# Revit family: Котел_ТЕРМОТЕХНИК_ТТ100-01_1-20 мВт
name_source: partatom
category: Оборудование
units: mm (PartAtom-declared; Revit-internal decimal feet)

## family parameters
Всегда вертикально = Да
Классификация = Нет
На основе рабочей плоскости = Нет
Общий = Нет
При загрузке вырезать с полостями = Нет
Размер круглого соединителя = Использовать диаметр
Тип детали = Нормальный
Точка расчета площади = Нет

## types (23) — shared parameters
G = 25 мм
URL = https://www.entroros.ru
Видимость_ВКЛ = Да
Видимость_ВЫКЛ = Нет
Изготовитель = ЭНТРОРОС
Ключевая пометка = https://www.entroros.ru
Код по классификатору = D3020100
Материал_Условный BOX = <По категории>
Описание = Котел ЭНТРОРОС ТЕРМОТЕХНИК ТТ100-01
Производитель = ЭНТРОРОС
Семейство заказано = ООО ЭНТРОРОС (entroros.ru)
Семейство оборудования = ТТ100-01
Семейство разработано = ООО DASBIM (dasbim.ru)
Ссылка на документацию = https://www.entroros.ru
Штуцер_Датчик дым.газов_D = G1/2-B
Штуцер_Датчик темп. воды на входе_D = G1/2-B
Штуцер_Датчик темп. воды на выходе_D = G1/2-B
Штуцер_Люк смотровой_D = 225х160
Штуцер_Слив конденсата_D = 25 мм
Штуцер_Слив конденсата_D_Формула = G1-B
Штуцер_Тягонапоромер_D = G1/2-B
Эксплуатационный КПД (%) не менее = 94
zero-valued in all types: Стоимость, Штуцер_Люк смотровой_А

## per-type parameters (varying)
- 01_1000_ef_406: B=1540 мм; H=1768 мм; L=3183 мм; А_Дверь_Смещение наружной грани=3038 мм; Аэродин. сопротивление (Па)=256; Дверь_052=Нет; Дверь_055=Нет; Дверь_151=Нет; Дверь_153=Нет; Дверь_154=Нет; Дверь_156=Нет; Дверь_206=Да; Дверь_208=Нет; Дверь_210=Нет; Дверь_212=Нет; Дверь_213=Нет; Комментарии к типоразмеру=1.0 мВт; Корпус_151=Нет; Корпус_152=Нет; Корпус_153=Нет; Корпус_154=Нет; Корпус_155=Нет; Корпус_156=Нет; Корпус_310=Нет; Корпус_311=Нет; Корпус_312=Нет; Корпус_313=Нет; Корпус_406=Да; Корпус_408=Нет; Корпус_409=Нет; Масса наполненного котла (кг)=5190; Масса сухого котла (кг)=3326; Ном. мощность (кВт)=1000; Подключение горелки=300; С_Ось котла=910 мм; Штуцер_Вход воды_D=125 мм; Штуцер_Вход воды_А=400 мм; Штуцер_Выход воды_D=125 мм; Штуцер_Выход воды_А=1038 мм; Штуцер_Выход дыма_D=350 мм; Штуцер_Выход дыма_В=1360 мм; Штуцер_Подключение горелки=300 мм; Штуцер_Пред.клапан1_D=50 мм; Штуцер_Пред.клапан1_А=430 мм; Штуцер_Пред.клапан2_D=50 мм; Штуцер_Пред.клапан2_а=300 мм; Штуцер_Слив воды_D=40 мм; Штуцер_Слив воды_D_Формула=G1/2-B; Штуцер_Слив воды_А=0 мм; Штуцер_Слив воды_В=86 мм; Штуцер_Слив конденсата_А=0 мм; Штуцер_Слив конденсата_В=231 мм
- 02_1500_ef_407: B=1540 мм; H=1768 мм; L=3183 мм; А_Дверь_Смещение наружной грани=3038 мм; Аэродин. сопротивление (Па)=673; Дверь_052=Нет; Дверь_055=Нет; Дверь_151=Нет; Дверь_153=Нет; Дверь_154=Нет; Дверь_156=Нет; Дверь_206=Да; Дверь_208=Нет; Дверь_210=Нет; Дверь_212=Нет; Дверь_213=Нет; Комментарии к типоразмеру=1.5 мВт; Корпус_151=Нет; Корпус_152=Нет; Корпус_153=Нет; Корпус_154=Нет; Корпус_155=Нет; Корпус_156=Нет; Корпус_310=Нет; Корпус_311=Нет; Корпус_312=Нет; Корпус_313=Нет; Корпус_406=Да; Корпус_408=Нет; Корпус_409=Нет; Масса наполненного котла (кг)=5293; Масса сухого котла (кг)=3429; Ном. мощность (кВт)=1500; Подключение горелки=300; С_Ось котла=910 мм; Штуцер_Вход воды_D=125 мм; Штуцер_Вход воды_А=400 мм; Штуцер_Выход воды_D=125 мм; Штуцер_Выход воды_А=1038 мм; Штуцер_Выход дыма_D=350 мм; Штуцер_Выход дыма_В=1360 мм; Штуцер_Подключение горелки=300 мм; Штуцер_Пред.клапан1_D=50 мм; Штуцер_Пред.клапан1_А=430 мм; Штуцер_Пред.клапан2_D=50 мм; Штуцер_Пред.клапан2_а=300 мм; Штуцер_Слив воды_D=40 мм; Штуцер_Слив воды_D_Формула=G1/2-B; Штуцер_Слив воды_А=0 мм; Штуцер_Слив воды_В=86 мм; Штуцер_Слив конденсата_А=0 мм; Штуцер_Слив конденсата_В=231 мм
- 03_2000_ef_408: B=1740 мм; H=1968 мм; L=3485 мм; А_Дверь_Смещение наружной грани=3340 мм; Аэродин. сопротивление (Па)=832; Дверь_052=Нет; Дверь_055=Нет; Дверь_151=Нет; Дверь_153=Нет; Дверь_154=Нет; Дверь_156=Нет; Дверь_206=Нет; Дверь_208=Да; Дверь_210=Нет; Дверь_212=Нет; Дверь_213=Нет; Комментарии к типоразмеру=2.0 мВт; Корпус_151=Нет; Корпус_152=Нет; Корпус_153=Нет; Корпус_154=Нет; Корпус_155=Нет; Корпус_156=Нет; Корпус_310=Нет; Корпус_311=Нет; Корпус_312=Нет; Корпус_313=Нет; Корпус_406=Нет; Корпус_408=Да; Корпус_409=Нет; Масса наполненного котла (кг)=7417; Масса сухого котла (кг)=4761; Ном. мощность (кВт)=2000; Подключение горелки=380; С_Ось котла=1010 мм; Штуцер_Вход воды_D=150 мм; Штуцер_Вход воды_А=550 мм; Штуцер_Выход воды_D=150 мм; Штуцер_Выход воды_А=820 мм; Штуцер_Выход дыма_D=500 мм; Штуцер_Выход дыма_В=1520 мм; Штуцер_Подключение горелки=380 мм; Штуцер_Пред.клапан1_D=65 мм; Штуцер_Пред.клапан1_А=1205 мм; Штуцер_Пред.клапан2_D=65 мм; Штуцер_Пред.клапан2_а=300 мм; Штуцер_Слив воды_D=40 мм; Штуцер_Слив воды_D_Формула=G1/2-B; Штуцер_Слив воды_А=0 мм; Штуцер_Слив воды_В=86 мм; Штуцер_Слив конденсата_А=0 мм; Штуцер_Слив конденсата_В=232 мм
- 04_2200_ef_4081: B=1740 мм; H=1968 мм; L=3485 мм; А_Дверь_Смещение наружной грани=3340 мм; Аэродин. сопротивление (Па)=1043; Дверь_052=Нет; Дверь_055=Нет; Дверь_151=Нет; Дверь_153=Нет; Дверь_154=Нет; Дверь_156=Нет; Дверь_206=Нет; Дверь_208=Да; Дверь_210=Нет; Дверь_212=Нет; Дверь_213=Нет; Комментарии к типоразмеру=2.2 мВт; Корпус_151=Нет; Корпус_152=Нет; Корпус_153=Нет; Корпус_154=Нет; Корпус_155=Нет; Корпус_156=Нет; Корпус_310=Нет; Корпус_311=Нет; Корпус_312=Нет; Корпус_313=Нет; Корпус_406=Нет; Корпус_408=Да; Корпус_409=Нет; Масса наполненного котла (кг)=7566; Масса сухого котла (кг)=4909; Ном. мощность (кВт)=2200; Подключение горелки=380; С_Ось котла=1010 мм; Штуцер_Вход воды_D=150 мм; Штуцер_Вход воды_А=550 мм; Штуцер_Выход воды_D=150 мм; Штуцер_Выход воды_А=820 мм; Штуцер_Выход дыма_D=500 мм; Штуцер_Выход дыма_В=1520 мм; Штуцер_Подключение горелки=380 мм; Штуцер_Пред.клапан1_D=65 мм; Штуцер_Пред.клапан1_А=1205 мм; Штуцер_Пред.клапан2_D=65 мм; Штуцер_Пред.клапан2_а=300 мм; Штуцер_Слив воды_D=40 мм; Штуцер_Слив воды_D_Формула=G1/2-B; Штуцер_Слив воды_А=0 мм; Штуцер_Слив воды_В=86 мм; Штуцер_Слив конденсата_А=0 мм; Штуцер_Слив конденсата_В=232 мм
- 05_2500_ef_409: B=1740 мм; H=1968 мм; L=3735 мм; А_Дверь_Смещение наружной грани=3590 мм; Аэродин. сопротивление (Па)=1030; Дверь_052=Нет; Дверь_055=Нет; Дверь_151=Нет; Дверь_153=Нет; Дверь_154=Нет; Дверь_156=Нет; Дверь_206=Нет; Дверь_208=Да; Дверь_210=Нет; Дверь_212=Нет; Дверь_213=Нет; Комментарии к типоразмеру=2.5 мВт; Корпус_151=Нет; Корпус_152=Нет; Корпус_153=Нет; Корпус_154=Нет; Корпус_155=Нет; Корпус_156=Нет; Корпус_310=Нет; Корпус_311=Нет; Корпус_312=Нет; Корпус_313=Нет; Корпус_406=Нет; Корпус_408=Нет; Корпус_409=Да; Масса наполненного котла (кг)=8124; Масса сухого котла (кг)=5385; Ном. мощность (кВт)=2500; Подключение горелки=380; С_Ось котла=1010 мм; Штуцер_Вход воды_D=150 мм; Штуцер_Вход воды_А=550 мм; Штуцер_Выход воды_D=150 мм; Штуцер_Выход воды_А=875 мм; Штуцер_Выход дыма_D=500 мм; Штуцер_Выход дыма_В=1520 мм; Штуцер_Подключение горелки=380 мм; Штуцер_Пред.клапан1_D=65 мм; Штуцер_Пред.клапан1_А=1400 мм; Штуцер_Пред.клапан2_D=65 мм; Штуцер_Пред.клапан2_а=300 мм; Штуцер_Слив воды_D=40 мм; Штуцер_Слив воды_D_Формула=G1/2-B; Штуцер_Слив воды_А=0 мм; Штуцер_Слив воды_В=86 мм; Штуцер_Слив конденсата_А=0 мм; Штуцер_Слив конденсата_В=232 мм
- 06_3000_ef_310: B=1940 мм; H=2168 мм; L=4134 мм; А_Дверь_Смещение наружной грани=3978 мм; Аэродин. сопротивление (Па)=895; Дверь_052=Нет; Дверь_055=Нет; Дверь_151=Нет; Дверь_153=Нет; Дверь_154=Нет; Дверь_156=Нет; Дверь_206=Нет; Дверь_208=Нет; Дверь_210=Да; Дверь_212=Нет; Дверь_213=Нет; Комментарии к типоразмеру=3.0 мВт; Корпус_151=Нет; Корпус_152=Нет; Корпус_153=Нет; Корпус_154=Нет; Корпус_155=Нет; Корпус_156=Нет; Корпус_310=Да; Корпус_311=Нет; Корпус_312=Нет; Корпус_313=Нет; Корпус_406=Нет; Корпус_408=Нет; Корпус_409=Нет; Масса наполненного котла (кг)=10993; Масса сухого котла (кг)=7102; Ном. мощность (кВт)=3000; Подключение горелки=450; С_Ось котла=1110 мм; Штуцер_Вход воды_D=200 мм; Штуцер_Вход воды_А=600 мм; Штуцер_Выход воды_D=200 мм; Штуцер_Выход воды_А=963 мм; Штуцер_Выход дыма_D=500 мм; Штуцер_Выход дыма_В=1720 мм; Штуцер_Подключение горелки=450 мм; Штуцер_Пред.клапан1_D=65 мм; Штуцер_Пред.клапан1_А=1600 мм; Штуцер_Пред.клапан2_D=65 мм; Штуцер_Пред.клапан2_а=300 мм; Штуцер_Слив воды_D=40 мм; Штуцер_Слив воды_D_Формула=G1/2-B; Штуцер_Слив воды_А=0 мм; Штуцер_Слив воды_В=116 мм; Штуцер_Слив конденсата_А=0 мм; Штуцер_Слив конденсата_В=233 мм
- 07_3200_ef_3101: B=1940 мм; H=2168 мм; L=4134 мм; А_Дверь_Смещение наружной грани=3978 мм; Аэродин. сопротивление (Па)=1046; Дверь_052=Нет; Дверь_055=Нет; Дверь_151=Нет; Дверь_153=Нет; Дверь_154=Нет; Дверь_156=Нет; Дверь_206=Нет; Дверь_208=Нет; Дверь_210=Да; Дверь_212=Нет; Дверь_213=Нет; Комментарии к типоразмеру=3.2 мВт; Корпус_151=Нет; Корпус_152=Нет; Корпус_153=Нет; Корпус_154=Нет; Корпус_155=Нет; Корпус_156=Нет; Корпус_310=Да; Корпус_311=Нет; Корпус_312=Нет; Корпус_313=Нет; Корпус_406=Нет; Корпус_408=Нет; Корпус_409=Нет; Масса наполненного котла (кг)=11213; Масса сухого котла (кг)=7322; Ном. мощность (кВт)=3200; Подключение горелки=450; С_Ось котла=1110 мм; Штуцер_Вход воды_D=200 мм; Штуцер_Вход воды_А=600 мм; Штуцер_Выход воды_D=200 мм; Штуцер_Выход воды_А=963 мм; Штуцер_Выход дыма_D=500 мм; Штуцер_Выход дыма_В=1720 мм; Штуцер_Подключение горелки=450 мм; Штуцер_Пред.клапан1_D=65 мм; Штуцер_Пред.клапан1_А=1600 мм; Штуцер_Пред.клапан2_D=65 мм; Штуцер_Пред.клапан2_а=300 мм; Штуцер_Слив воды_D=40 мм; Штуцер_Слив воды_D_Формула=G1/2-B; Штуцер_Слив воды_А=0 мм; Штуцер_Слив воды_В=116 мм; Штуцер_Слив конденсата_А=0 мм; Штуцер_Слив конденсата_В=233 мм
- 08_3500_ef_311: B=1940 мм; H=2168 мм; L=4532 мм; А_Дверь_Смещение наружной грани=4378 мм; Аэродин. сопротивление (Па)=1245; Дверь_052=Нет; Дверь_055=Нет; Дверь_151=Нет; Дверь_153=Нет; Дверь_154=Нет; Дверь_156=Нет; Дверь_206=Нет; Дверь_208=Нет; Дверь_210=Да; Дверь_212=Нет; Дверь_213=Нет; Комментарии к типоразмеру=3.5 мВт; Корпус_151=Нет; Корпус_152=Нет; Корпус_153=Нет; Корпус_154=Нет; Корпус_155=Нет; Корпус_156=Нет; Корпус_310=Нет; Корпус_311=Да; Корпус_312=Нет; Корпус_313=Нет; Корпус_406=Нет; Корпус_408=Нет; Корпус_409=Нет; Масса наполненного котла (кг)=12363; Масса сухого котла (кг)=7971; Ном. мощность (кВт)=3500; Подключение горелки=450; С_Ось котла=1110 мм; Штуцер_Вход воды_D=200 мм; Штуцер_Вход воды_А=600 мм; Штуцер_Выход воды_D=200 мм; Штуцер_Выход воды_А=1013 мм; Штуцер_Выход дыма_D=500 мм; Штуцер_Выход дыма_В=1720 мм; Штуцер_Подключение горелки=450 мм; Штуцер_Пред.клапан1_D=65 мм; Штуцер_Пред.клапан1_А=1950 мм; Штуцер_Пред.клапан2_D=65 мм; Штуцер_Пред.клапан2_а=300 мм; Штуцер_Слив воды_D=40 мм; Штуцер_Слив воды_D_Формула=G1/2-B; Штуцер_Слив воды_А=0 мм; Штуцер_Слив воды_В=116 мм; Штуцер_Слив конденсата_А=0 мм; Штуцер_Слив конденсата_В=233 мм
- 09_4200_ef_312: B=2100 мм; H=2328 мм; L=4831 мм; А_Дверь_Смещение наружной грани=4674 мм; Аэродин. сопротивление (Па)=1213; Дверь_052=Нет; Дверь_055=Нет; Дверь_151=Нет; Дверь_153=Нет; Дверь_154=Нет; Дверь_156=Нет; Дверь_206=Нет; Дверь_208=Нет; Дверь_210=Нет; Дверь_212=Да; Дверь_213=Нет; Комментарии к типоразмеру=4.2 мВт; Корпус_151=Нет; Корпус_152=Нет; Корпус_153=Нет; Корпус_154=Нет; Корпус_155=Нет; Корпус_156=Нет; Корпус_310=Нет; Корпус_311=Нет; Корпус_312=Да; Корпус_313=Нет; Корпус_406=Нет; Корпус_408=Нет; Корпус_409=Нет; Масса наполненного котла (кг)=14921; Масса сухого котла (кг)=7980; Ном. мощность (кВт)=4200; Подключение горелки=450; С_Ось котла=1205 мм; Штуцер_Вход воды_D=200 мм; Штуцер_Вход воды_А=700 мм; Штуцер_Выход воды_D=200 мм; Штуцер_Выход воды_А=959 мм; Штуцер_Выход дыма_D=650 мм; Штуцер_Выход дыма_В=1805 мм; Штуцер_Подключение горелки=450 мм; Штуцер_Пред.клапан1_D=80 мм; Штуцер_Пред.клапан1_А=2100 мм; Штуцер_Пред.клапан2_D=80 мм; Штуцер_Пред.клапан2_а=300 мм; Штуцер_Слив воды_D=40 мм; Штуцер_Слив воды_D_Формула=G1/2-B; Штуцер_Слив воды_А=0 мм; Штуцер_Слив воды_В=119 мм; Штуцер_Слив конденсата_А=0 мм; Штуцер_Слив конденсата_В=266 мм
- 10_5000_ef_3121: B=2100 мм; H=2328 мм; L=4831 мм; А_Дверь_Смещение наружной грани=4674 мм; Аэродин. сопротивление (Па)=1806; Дверь_052=Нет; Дверь_055=Нет; Дверь_151=Нет; Дверь_153=Нет; Дверь_154=Нет; Дверь_156=Нет; Дверь_206=Нет; Дверь_208=Нет; Дверь_210=Нет; Дверь_212=Да; Дверь_213=Нет; Комментарии к типоразмеру=5.0 мВт; Корпус_151=Нет; Корпус_152=Нет; Корпус_153=Нет; Корпус_154=Нет; Корпус_155=Нет; Корпус_156=Нет; Корпус_310=Нет; Корпус_311=Нет; Корпус_312=Да; Корпус_313=Нет; Корпус_406=Нет; Корпус_408=Нет; Корпус_409=Нет; Масса наполненного котла (кг)=15201; Масса сухого котла (кг)=10083; Ном. мощность (кВт)=5000; Подключение горелки=450; С_Ось котла=1205 мм; Штуцер_Вход воды_D=200 мм; Штуцер_Вход воды_А=700 мм; Штуцер_Выход воды_D=200 мм; Штуцер_Выход воды_А=959 мм; Штуцер_Выход дыма_D=650 мм; Штуцер_Выход дыма_В=1805 мм; Штуцер_Подключение горелки=450 мм; Штуцер_Пред.клапан1_D=80 мм; Штуцер_Пред.клапан1_А=2100 мм; Штуцер_Пред.клапан2_D=80 мм; Штуцер_Пред.клапан2_а=300 мм; Штуцер_Слив воды_D=40 мм; Штуцер_Слив воды_D_Формула=G1/2-B; Штуцер_Слив воды_А=0 мм; Штуцер_Слив воды_В=119 мм; Штуцер_Слив конденсата_А=0 мм; Штуцер_Слив конденсата_В=266 мм
- 11_5400_ef_313: B=2200 мм; H=2438 мм; L=5103 мм; А_Дверь_Смещение наружной грани=4963 мм; Аэродин. сопротивление (Па)=1058; Дверь_052=Нет; Дверь_055=Нет; Дверь_151=Нет; Дверь_153=Нет; Дверь_154=Нет; Дверь_156=Нет; Дверь_206=Нет; Дверь_208=Нет; Дверь_210=Нет; Дверь_212=Нет; Дверь_213=Да; Комментарии к типоразмеру=5.4 мВт; Корпус_151=Нет; Корпус_152=Нет; Корпус_153=Нет; Корпус_154=Нет; Корпус_155=Нет; Корпус_156=Нет; Корпус_310=Нет; Корпус_311=Нет; Корпус_312=Нет; Корпус_313=Да; Корпус_406=Нет; Корпус_408=Нет; Корпус_409=Нет; Масса наполненного котла (кг)=16781; Масса сухого котла (кг)=11247; Ном. мощность (кВт)=5400; Подключение горелки=450; С_Ось котла=1262 мм; Штуцер_Вход воды_D=250 мм; Штуцер_Вход воды_А=800 мм; Штуцер_Выход воды_D=250 мм; Штуцер_Выход воды_А=1146 мм; Штуцер_Выход дыма_D=650 мм; Штуцер_Выход дыма_В=1890 мм; Штуцер_Подключение горелки=450 мм; Штуцер_Пред.клапан1_D=80 мм; Штуцер_Пред.клапан1_А=2100 мм; Штуцер_Пред.клапан2_D=80 мм; Штуцер_Пред.клапан2_а=300 мм; Штуцер_Слив воды_D=50 мм; Штуцер_Слив воды_D_Формула=50; Штуцер_Слив воды_А=0 мм; Штуцер_Слив воды_В=139 мм; Штуцер_Слив конденсата_А=0 мм; Штуцер_Слив конденсата_В=263 мм
- 12_6000_ef_3131: B=2200 мм; H=2438 мм; L=5103 мм; А_Дверь_Смещение наружной грани=4963 мм; Аэродин. сопротивление (Па)=1352; Дверь_052=Нет; Дверь_055=Нет; Дверь_151=Нет; Дверь_153=Нет; Дверь_154=Нет; Дверь_156=Нет; Дверь_206=Нет; Дверь_208=Нет; Дверь_210=Нет; Дверь_212=Нет; Дверь_213=Да; Комментарии к типоразмеру=6.0 мВт; Корпус_151=Нет; Корпус_152=Нет; Корпус_153=Нет; Корпус_154=Нет; Корпус_155=Нет; Корпус_156=Нет; Корпус_310=Нет; Корпус_311=Нет; Корпус_312=Нет; Корпус_313=Да; Корпус_406=Нет; Корпус_408=Нет; Корпус_409=Нет; Масса наполненного котла (кг)=17572; Масса сухого котла (кг)=11595; Ном. мощность (кВт)=6000; Подключение горелки=450; С_Ось котла=1262 мм; Штуцер_Вход воды_D=250 мм; Штуцер_Вход воды_А=800 мм; Штуцер_Выход воды_D=250 мм; Штуцер_Выход воды_А=1146 мм; Штуцер_Выход дыма_D=650 мм; Штуцер_Выход дыма_В=1890 мм; Штуцер_Подключение горелки=450 мм; Штуцер_Пред.клапан1_D=80 мм; Штуцер_Пред.клапан1_А=2100 мм; Штуцер_Пред.клапан2_D=80 мм; Штуцер_Пред.клапан2_а=300 мм; Штуцер_Слив воды_D=50 мм; Штуцер_Слив воды_D_Формула=50; Штуцер_Слив воды_А=0 мм; Штуцер_Слив воды_В=139 мм; Штуцер_Слив конденсата_А=0 мм; Штуцер_Слив конденсата_В=263 мм
- 13_6500_ef_151: B=2360 мм; H=2574 мм; L=5412 мм; А_Дверь_Смещение наружной грани=5261 мм; Аэродин. сопротивление (Па)=1123; Дверь_052=Нет; Дверь_055=Нет; Дверь_151=Да; Дверь_153=Нет; Дверь_154=Нет; Дверь_156=Нет; Дверь_206=Нет; Дверь_208=Нет; Дверь_210=Нет; Дверь_212=Нет; Дверь_213=Нет; Комментарии к типоразмеру=6.5 мВт; Корпус_151=Да; Корпус_152=Нет; Корпус_153=Нет; Корпус_154=Нет; Корпус_155=Нет; Корпус_156=Нет; Корпус_310=Нет; Корпус_311=Нет; Корпус_312=Нет; Корпус_313=Нет; Корпус_406=Нет; Корпус_408=Нет; Корпус_409=Нет; Масса наполненного котла (кг)=21299; Масса сухого котла (кг)=14071; Ном. мощность (кВт)=6500; Подключение горелки=500; С_Ось котла=1314 мм; Штуцер_Вход воды_D=250 мм; Штуцер_Вход воды_А=900 мм; Штуцер_Выход воды_D=250 мм; Штуцер_Выход воды_А=1134 мм; Штуцер_Выход дыма_D=800 мм; Штуцер_Выход дыма_В=1970 мм; Штуцер_Подключение горелки=500 мм; Штуцер_Пред.клапан1_D=100 мм; Штуцер_Пред.клапан1_А=1970 мм; Штуцер_Пред.клапан2_D=100 мм; Штуцер_Пред.клапан2_а=370 мм; Штуцер_Слив воды_D=50 мм; Штуцер_Слив воды_D_Формула=50; Штуцер_Слив воды_А=91 мм; Штуцер_Слив воды_В=120 мм; Штуцер_Слив конденсата_А=0 мм; Штуцер_Слив конденсата_В=236 мм
- 14_7000_ef_1511: B=2360 мм; H=2574 мм; L=5412 мм; А_Дверь_Смещение наружной грани=5261 мм; Аэродин. сопротивление (Па)=1335; Дверь_052=Нет; Дверь_055=Нет; Дверь_151=Да; Дверь_153=Нет; Дверь_154=Нет; Дверь_156=Нет; Дверь_206=Нет; Дверь_208=Нет; Дверь_210=Нет; Дверь_212=Нет; Дверь_213=Нет; Комментарии к типоразмеру=7.0 мВт; Корпус_151=Да; Корпус_152=Нет; Корпус_153=Нет; Корпус_154=Нет; Корпус_155=Нет; Корпус_156=Нет; Корпус_310=Нет; Корпус_311=Нет; Корпус_312=Нет; Корпус_313=Нет; Корпус_406=Нет; Корпус_408=Нет; Корпус_409=Нет; Масса наполненного котла (кг)=21735; Масса сухого котла (кг)=14507; Ном. мощность (кВт)=7000; Подключение горелки=500; С_Ось котла=1314 мм; Штуцер_Вход воды_D=250 мм; Штуцер_Вход воды_А=900 мм; Штуцер_Выход воды_D=250 мм; Штуцер_Выход воды_А=1134 мм; Штуцер_Выход дыма_D=800 мм; Штуцер_Выход дыма_В=1970 мм; Штуцер_Подключение горелки=500 мм; Штуцер_Пред.клапан1_D=100 мм; Штуцер_Пред.клапан1_А=1970 мм; Штуцер_Пред.клапан2_D=100 мм; Штуцер_Пред.клапан2_а=370 мм; Штуцер_Слив воды_D=50 мм; Штуцер_Слив воды_D_Формула=50; Штуцер_Слив воды_А=91 мм; Штуцер_Слив воды_В=120 мм; Штуцер_Слив конденсата_А=0 мм; Штуцер_Слив конденсата_В=236 мм
- 15_8000_ef_152: B=2500 мм; H=2710 мм; L=5805 мм; А_Дверь_Смещение наружной грани=5648 мм; Аэродин. сопротивление (Па)=1251; Дверь_052=Да; Дверь_055=Нет; Дверь_151=Нет; Дверь_153=Нет; Дверь_154=Нет; Дверь_156=Нет; Дверь_206=Нет; Дверь_208=Нет; Дверь_210=Нет; Дверь_212=Нет; Дверь_213=Нет; Комментарии к типоразмеру=8.0 мВт; Корпус_151=Нет; Корпус_152=Да; Корпус_153=Нет; Корпус_154=Нет; Корпус_155=Нет; Корпус_156=Нет; Корпус_310=Нет; Корпус_311=Нет; Корпус_312=Нет; Корпус_313=Нет; Корпус_406=Нет; Корпус_408=Нет; Корпус_409=Нет; Масса наполненного котла (кг)=25867; Масса сухого котла (кг)=16961; Ном. мощность (кВт)=8000; Подключение горелки=590; С_Ось котла=1370 мм; Штуцер_Вход воды_D=300 мм; Штуцер_Вход воды_А=1000 мм; Штуцер_Выход воды_D=300 мм; Штуцер_Выход воды_А=1215 мм; Штуцер_Выход дыма_D=800 мм; Штуцер_Выход дыма_В=2070 мм; Штуцер_Подключение горелки=590 мм; Штуцер_Пред.клапан1_D=100 мм; Штуцер_Пред.клапан1_А=1990 мм; Штуцер_Пред.клапан2_D=100 мм; Штуцер_Пред.клапан2_а=500 мм; Штуцер_Слив воды_D=50 мм; Штуцер_Слив воды_D_Формула=50; Штуцер_Слив воды_А=0 мм; Штуцер_Слив воды_В=82 мм; Штуцер_Слив конденсата_А=0 мм; Штуцер_Слив конденсата_В=213 мм
- 16_8700_ef_1521: B=2500 мм; H=2710 мм; L=5805 мм; А_Дверь_Смещение наружной грани=5648 мм; Аэродин. сопротивление (Па)=1524; Дверь_052=Да; Дверь_055=Нет; Дверь_151=Нет; Дверь_153=Нет; Дверь_154=Нет; Дверь_156=Нет; Дверь_206=Нет; Дверь_208=Нет; Дверь_210=Нет; Дверь_212=Нет; Дверь_213=Нет; Комментарии к типоразмеру=8.7 мВт; Корпус_151=Нет; Корпус_152=Да; Корпус_153=Нет; Корпус_154=Нет; Корпус_155=Нет; Корпус_156=Нет; Корпус_310=Нет; Корпус_311=Нет; Корпус_312=Нет; Корпус_313=Нет; Корпус_406=Нет; Корпус_408=Нет; Корпус_409=Нет; Масса наполненного котла (кг)=26219; Масса сухого котла (кг)=17486; Ном. мощность (кВт)=8700; Подключение горелки=590; С_Ось котла=1370 мм; Штуцер_Вход воды_D=300 мм; Штуцер_Вход воды_А=1000 мм; Штуцер_Выход воды_D=300 мм; Штуцер_Выход воды_А=1215 мм; Штуцер_Выход дыма_D=800 мм; Штуцер_Выход дыма_В=2070 мм; Штуцер_Подключение горелки=590 мм; Штуцер_Пред.клапан1_D=100 мм; Штуцер_Пред.клапан1_А=1990 мм; Штуцер_Пред.клапан2_D=100 мм; Штуцер_Пред.клапан2_а=500 мм; Штуцер_Слив воды_D=50 мм; Штуцер_Слив воды_D_Формула=50; Штуцер_Слив воды_А=0 мм; Штуцер_Слив воды_В=82 мм; Штуцер_Слив конденсата_А=0 мм; Штуцер_Слив конденсата_В=213 мм
- 17_10000_ef_153: B=2680 мм; H=2862 мм; L=6440 мм; А_Дверь_Смещение наружной грани=6290 мм; Аэродин. сопротивление (Па)=1461; Дверь_052=Нет; Дверь_055=Нет; Дверь_151=Нет; Дверь_153=Да; Дверь_154=Нет; Дверь_156=Нет; Дверь_206=Нет; Дверь_208=Нет; Дверь_210=Нет; Дверь_212=Нет; Дверь_213=Нет; Комментарии к типоразмеру=10.0 мВт; Корпус_151=Нет; Корпус_152=Нет; Корпус_153=Да; Корпус_154=Нет; Корпус_155=Нет; Корпус_156=Нет; Корпус_310=Нет; Корпус_311=Нет; Корпус_312=Нет; Корпус_313=Нет; Корпус_406=Нет; Корпус_408=Нет; Корпус_409=Нет; Масса наполненного котла (кг)=32600; Масса сухого котла (кг)=20415; Ном. мощность (кВт)=10000; Подключение горелки=590; С_Ось котла=1450 мм; Штуцер_Вход воды_D=300 мм; Штуцер_Вход воды_А=1400 мм; Штуцер_Выход воды_D=300 мм; Штуцер_Выход воды_А=1217 мм; Штуцер_Выход дыма_D=900 мм; Штуцер_Выход дыма_В=2130 мм; Штуцер_Подключение горелки=590 мм; Штуцер_Пред.клапан1_D=125 мм; Штуцер_Пред.клапан1_А=2350 мм; Штуцер_Пред.клапан2_D=125 мм; Штуцер_Пред.клапан2_а=500 мм; Штуцер_Слив воды_D=50 мм; Штуцер_Слив воды_D_Формула=50; Штуцер_Слив воды_А=0 мм; Штуцер_Слив воды_В=91 мм; Штуцер_Слив конденсата_А=0 мм; Штуцер_Слив конденсата_В=290 мм
- 18_12000_ef_154: B=2860 мм; H=3074 мм; L=6954 мм; А_Дверь_Смещение наружной грани=6805 мм; Аэродин. сопротивление (Па)=1481; Дверь_052=Нет; Дверь_055=Нет; Дверь_151=Нет; Дверь_153=Нет; Дверь_154=Да; Дверь_156=Нет; Дверь_206=Нет; Дверь_208=Нет; Дверь_210=Нет; Дверь_212=Нет; Дверь_213=Нет; Комментарии к типоразмеру=12.0 мВт; Корпус_151=Нет; Корпус_152=Нет; Корпус_153=Нет; Корпус_154=Да; Корпус_155=Нет; Корпус_156=Нет; Корпус_310=Нет; Корпус_311=Нет; Корпус_312=Нет; Корпус_313=Нет; Корпус_406=Нет; Корпус_408=Нет; Корпус_409=Нет; Масса наполненного котла (кг)=39909; Масса сухого котла (кг)=23908; Ном. мощность (кВт)=12000; Подключение горелки=730; С_Ось котла=1564 мм; Штуцер_Вход воды_D=350 мм; Штуцер_Вход воды_А=1600 мм; Штуцер_Выход воды_D=350 мм; Штуцер_Выход воды_А=1506 мм; Штуцер_Выход дыма_D=1000 мм; Штуцер_Выход дыма_В=2364 мм; Штуцер_Подключение горелки=730 мм; Штуцер_Пред.клапан1_D=125 мм; Штуцер_Пред.клапан1_А=2440 мм; Штуцер_Пред.клапан2_D=125 мм; Штуцер_Пред.клапан2_а=500 мм; Штуцер_Слив воды_D=50 мм; Штуцер_Слив воды_D_Формула=50; Штуцер_Слив воды_А=0 мм; Штуцер_Слив воды_В=105 мм; Штуцер_Слив конденсата_А=94 мм; Штуцер_Слив конденсата_В=226 мм
- 19_13000_ef_1541: B=2860 мм; H=3074 мм; L=6954 мм; А_Дверь_Смещение наружной грани=6805 мм; Аэродин. сопротивление (Па)=1790; Дверь_052=Нет; Дверь_055=Нет; Дверь_151=Нет; Дверь_153=Нет; Дверь_154=Да; Дверь_156=Нет; Дверь_206=Нет; Дверь_208=Нет; Дверь_210=Нет; Дверь_212=Нет; Дверь_213=Нет; Комментарии к типоразмеру=13.0 мВт; Корпус_151=Нет; Корпус_152=Нет; Корпус_153=Нет; Корпус_154=Да; Корпус_155=Нет; Корпус_156=Нет; Корпус_310=Нет; Корпус_311=Нет; Корпус_312=Нет; Корпус_313=Нет; Корпус_406=Нет; Корпус_408=Нет; Корпус_409=Нет; Масса наполненного котла (кг)=40648; Масса сухого котла (кг)=24648; Ном. мощность (кВт)=13000; Подключение горелки=730; С_Ось котла=1564 мм; Штуцер_Вход воды_D=350 мм; Штуцер_Вход воды_А=1600 мм; Штуцер_Выход воды_D=350 мм; Штуцер_Выход воды_А=1506 мм; Штуцер_Выход дыма_D=1000 мм; Штуцер_Выход дыма_В=2364 мм; Штуцер_Подключение горелки=730 мм; Штуцер_Пред.клапан1_D=125 мм; Штуцер_Пред.клапан1_А=2440 мм; Штуцер_Пред.клапан2_D=125 мм; Штуцер_Пред.клапан2_а=500 мм; Штуцер_Слив воды_D=50 мм; Штуцер_Слив воды_D_Формула=50; Штуцер_Слив воды_А=0 мм; Штуцер_Слив воды_В=105 мм; Штуцер_Слив конденсата_А=94 мм; Штуцер_Слив конденсата_В=226 мм
- 20_15000_ef_155: B=3060 мм; H=3276 мм; L=7608 мм; А_Дверь_Смещение наружной грани=7461 мм; Аэродин. сопротивление (Па)=1798; Дверь_052=Нет; Дверь_055=Да; Дверь_151=Нет; Дверь_153=Нет; Дверь_154=Нет; Дверь_156=Нет; Дверь_206=Нет; Дверь_208=Нет; Дверь_210=Нет; Дверь_212=Нет; Дверь_213=Нет; Комментарии к типоразмеру=15.0 мВт; Корпус_151=Нет; Корпус_152=Нет; Корпус_153=Нет; Корпус_154=Нет; Корпус_155=Да; Корпус_156=Нет; Корпус_310=Нет; Корпус_311=Нет; Корпус_312=Нет; Корпус_313=Нет; Корпус_406=Нет; Корпус_408=Нет; Корпус_409=Нет; Масса наполненного котла (кг)=49820; Масса сухого котла (кг)=29820; Ном. мощность (кВт)=15000; Подключение горелки=730; С_Ось котла=1664 мм; Штуцер_Вход воды_D=400 мм; Штуцер_Вход воды_А=2000 мм; Штуцер_Выход воды_D=400 мм; Штуцер_Выход воды_А=1396 мм; Штуцер_Выход дыма_D=1000 мм; Штуцер_Выход дыма_В=2514 мм; Штуцер_Подключение горелки=730 мм; Штуцер_Пред.клапан1_D=125 мм; Штуцер_Пред.клапан1_А=2550 мм; Штуцер_Пред.клапан2_D=125 мм; Штуцер_Пред.клапан2_а=600 мм; Штуцер_Слив воды_D=50 мм; Штуцер_Слив воды_D_Формула=50; Штуцер_Слив воды_А=0 мм; Штуцер_Слив воды_В=109 мм; Штуцер_Слив конденсата_А=94 мм; Штуцер_Слив конденсата_В=230 мм
- 21_16500_ef_1551: B=3060 мм; H=3276 мм; L=7608 мм; А_Дверь_Смещение наружной грани=7461 мм; Аэродин. сопротивление (Па)=2245; Дверь_052=Нет; Дверь_055=Да; Дверь_151=Нет; Дверь_153=Нет; Дверь_154=Нет; Дверь_156=Нет; Дверь_206=Нет; Дверь_208=Нет; Дверь_210=Нет; Дверь_212=Нет; Дверь_213=Нет; Комментарии к типоразмеру=16.5 мВт; Корпус_151=Нет; Корпус_152=Нет; Корпус_153=Нет; Корпус_154=Нет; Корпус_155=Да; Корпус_156=Нет; Корпус_310=Нет; Корпус_311=Нет; Корпус_312=Нет; Корпус_313=Нет; Корпус_406=Нет; Корпус_408=Нет; Корпус_409=Нет; Масса наполненного котла (кг)=50743; Масса сухого котла (кг)=30743; Ном. мощность (кВт)=16500; Подключение горелки=730; С_Ось котла=1664 мм; Штуцер_Вход воды_D=400 мм; Штуцер_Вход воды_А=2000 мм; Штуцер_Выход воды_D=400 мм; Штуцер_Выход воды_А=1396 мм; Штуцер_Выход дыма_D=1000 мм; Штуцер_Выход дыма_В=2514 мм; Штуцер_Подключение горелки=730 мм; Штуцер_Пред.клапан1_D=125 мм; Штуцер_Пред.клапан1_А=2550 мм; Штуцер_Пред.клапан2_D=125 мм; Штуцер_Пред.клапан2_а=600 мм; Штуцер_Слив воды_D=50 мм; Штуцер_Слив воды_D_Формула=50; Штуцер_Слив воды_А=0 мм; Штуцер_Слив воды_В=109 мм; Штуцер_Слив конденсата_А=94 мм; Штуцер_Слив конденсата_В=230 мм
- 22_18000_ef_156: B=3390 мм; H=3606 мм; L=8064 мм; А_Дверь_Смещение наружной грани=7919 мм; Аэродин. сопротивление (Па)=1375; Дверь_052=Нет; Дверь_055=Нет; Дверь_151=Нет; Дверь_153=Нет; Дверь_154=Нет; Дверь_156=Да; Дверь_206=Нет; Дверь_208=Нет; Дверь_210=Нет; Дверь_212=Нет; Дверь_213=Нет; Комментарии к типоразмеру=18.0 мВт; Корпус_151=Нет; Корпус_152=Нет; Корпус_153=Нет; Корпус_154=Нет; Корпус_155=Нет; Корпус_156=Да; Корпус_310=Нет; Корпус_311=Нет; Корпус_312=Нет; Корпус_313=Нет; Корпус_406=Нет; Корпус_408=Нет; Корпус_409=Нет; Масса наполненного котла (кг)=63540; Масса сухого котла (кг)=38798; Ном. мощность (кВт)=18000; Подключение горелки=740; С_Ось котла=1829 мм; Штуцер_Вход воды_D=400 мм; Штуцер_Вход воды_А=2000 мм; Штуцер_Выход воды_D=400 мм; Штуцер_Выход воды_А=1854 мм; Штуцер_Выход дыма_D=1000 мм; Штуцер_Выход дыма_В=2679 мм; Штуцер_Подключение горелки=740 мм; Штуцер_Пред.клапан1_D=125 мм; Штуцер_Пред.клапан1_А=2550 мм; Штуцер_Пред.клапан2_D=125 мм; Штуцер_Пред.клапан2_а=600 мм; Штуцер_Слив воды_D=50 мм; Штуцер_Слив воды_D_Формула=50; Штуцер_Слив воды_А=0 мм; Штуцер_Слив воды_В=109 мм; Штуцер_Слив конденсата_А=94 мм; Штуцер_Слив конденсата_В=226 мм
- 23_20000_ef_1561: B=3390 мм; H=3606 мм; L=8064 мм; А_Дверь_Смещение наружной грани=7919 мм; Аэродин. сопротивление (Па)=1754; Дверь_052=Нет; Дверь_055=Нет; Дверь_151=Нет; Дверь_153=Нет; Дверь_154=Нет; Дверь_156=Да; Дверь_206=Нет; Дверь_208=Нет; Дверь_210=Нет; Дверь_212=Нет; Дверь_213=Нет; Комментарии к типоразмеру=20.0 мВт; Корпус_151=Нет; Корпус_152=Нет; Корпус_153=Нет; Корпус_154=Нет; Корпус_155=Нет; Корпус_156=Да; Корпус_310=Нет; Корпус_311=Нет; Корпус_312=Нет; Корпус_313=Нет; Корпус_406=Нет; Корпус_408=Нет; Корпус_409=Нет; Масса наполненного котла (кг)=64740; Масса сухого котла (кг)=39998; Ном. мощность (кВт)=20000; Подключение горелки=740; С_Ось котла=1829 мм; Штуцер_Вход воды_D=400 мм; Штуцер_Вход воды_А=2000 мм; Штуцер_Выход воды_D=400 мм; Штуцер_Выход воды_А=1854 мм; Штуцер_Выход дыма_D=1000 мм; Штуцер_Выход дыма_В=2679 мм; Штуцер_Подключение горелки=740 мм; Штуцер_Пред.клапан1_D=125 мм; Штуцер_Пред.клапан1_А=2550 мм; Штуцер_Пред.клапан2_D=125 мм; Штуцер_Пред.клапан2_а=600 мм; Штуцер_Слив воды_D=50 мм; Штуцер_Слив воды_D_Формула=50; Штуцер_Слив воды_А=0 мм; Штуцер_Слив воды_В=109 мм; Штуцер_Слив конденсата_А=94 мм; Штуцер_Слив конденсата_В=226 мм
